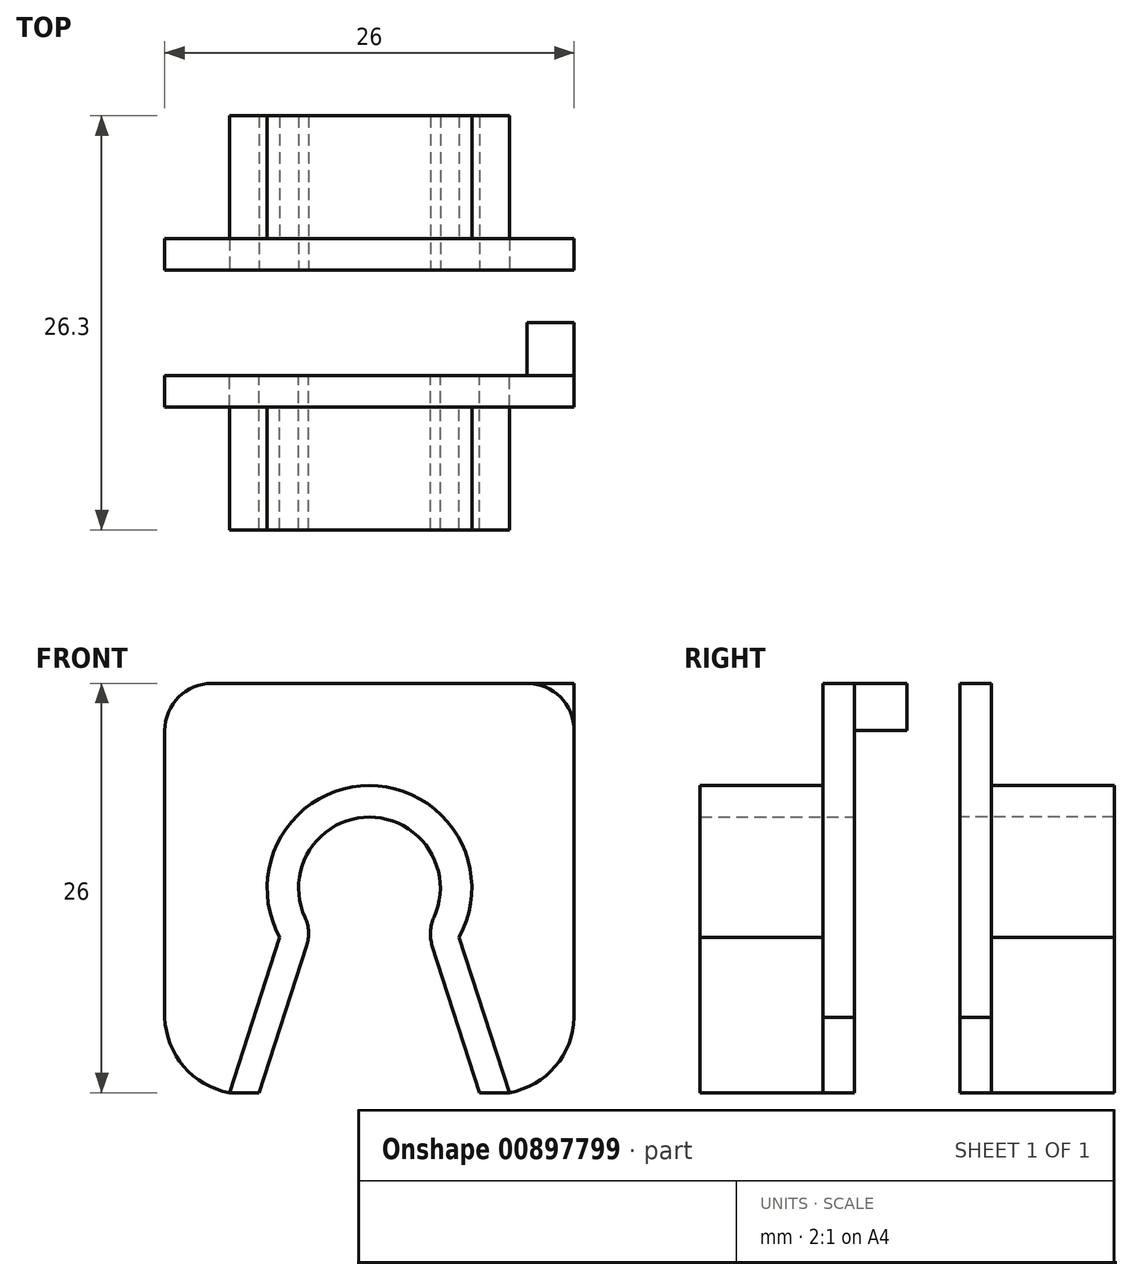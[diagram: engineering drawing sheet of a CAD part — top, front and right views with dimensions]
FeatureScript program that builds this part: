
annotation { "Feature Type Name" : "Feature", "Feature Type Description" : "" }
export const myFeature = defineFeature(function(context is Context, id is Id, definition is map)
    precondition{}
    {
        {
            var Q0;
            Q0=qCreatedBy(makeId("Front.planeOp"),FACE);
            var sketch = newSketch(context, id + "F0", { "sketchPlane" : qUnion([Q0])});
            skLineSegment(sketch, "E0.bottom", {"start": v(-13, 13) * mm, "end": v(13, 13) * mm});
            skLineSegment(sketch, "E0.top", {"start": v(-13, -13) * mm, "end": v(13, -13) * mm});
            skLineSegment(sketch, "E0.left", {"start": v(-13, 13) * mm, "end": v(-13, -13) * mm});
            skLineSegment(sketch, "E0.right", {"start": v(13, 13) * mm, "end": v(13, -13) * mm});
            skPoint(sketch, "E0.middle", {"position": v(0, 0) * mm});
            skCircle(sketch, "E1", {"center": v(0, 0) * mm, "radius": 4.5 * mm});
            skLineSegment(sketch, "E2", {"start": v(3.65, -2.63) * mm, "end": v(7, -13) * mm});
            skLineSegment(sketch, "E3", {"start": v(-3.65, -2.63) * mm, "end": v(-7, -13) * mm});
            skLineSegment(sketch, "E4", {"start": v(-4.42, 0.83) * mm, "end": v(-8.9, -13) * mm});
            skLineSegment(sketch, "E5", {"start": v(4.42, 0.83) * mm, "end": v(8.9, -13) * mm});
            skCircle(sketch, "E6", {"center": v(0, 0) * mm, "radius": 6.5 * mm});
            skLineSegment(sketch, "E7", {"start": v(-13, -8.21) * mm, "end": v(13, -8.21) * mm, "construction": true});
            skArc(sketch, "E8", {"start": v(-13, -8.21) * mm, "mid": v(-11.8, -11.34) * mm, "end": v(-8.9, -13) * mm});
            skArc(sketch, "E9", {"start": v(8.9, -13) * mm, "mid": v(11.8, -11.34) * mm, "end": v(13, -8.21) * mm});
            skSolve(sketch);
        }
        {
            var Q0;
            {var subQ0=sQuery(id+"F0.wireOp",EDGE,"E4");var subQ1=sQuery(id+"F0.wireOp",EDGE,"E1");var subQ2=makeQuery(id+"F0.imprint","INTERSECT",VERTEX,{"derivedFrom":[subQ1,subQ0]});Q0=makeQuery(id+"F0.imprint","IMPRINT",FACE,{"disambiguationData":[TD([[makeQuery(id+"F0.imprint","IMPRINT",EDGE,{"disambiguationData":[TD([[subQ2,1.0]])],"derivedFrom":subQ1}),-1.0]])]});}
            var Q1;
            {var subQ0=sQuery(id+"F0.wireOp",EDGE,"E3");var subQ1=sQuery(id+"F0.wireOp",EDGE,"E1");var subQ2=makeQuery(id+"F0.imprint","INTERSECT",VERTEX,{"derivedFrom":[subQ1,subQ0]});Q1=makeQuery(id+"F0.imprint","IMPRINT",FACE,{"disambiguationData":[TD([[makeQuery(id+"F0.imprint","IMPRINT",EDGE,{"disambiguationData":[TD([[subQ2,1.0]])],"derivedFrom":subQ1}),-1.0]])]});}
            var Q2;
            {var subQ0=sQuery(id+"F0.wireOp",EDGE,"E3");var subQ1=sQuery(id+"F0.wireOp",EDGE,"E0.top");var subQ2=makeQuery(id+"F0.imprint","INTERSECT",VERTEX,{"derivedFrom":[subQ1,subQ0]});Q2=makeQuery(id+"F0.imprint","IMPRINT",FACE,{"disambiguationData":[TD([[makeQuery(id+"F0.imprint","IMPRINT",EDGE,{"disambiguationData":[TD([[subQ2,1.0]])],"derivedFrom":subQ0}),-1.0]])]});}
            var Q3;
            {var subQ0=sQuery(id+"F0.wireOp",EDGE,"E2");var subQ1=sQuery(id+"F0.wireOp",EDGE,"E0.top");var subQ2=makeQuery(id+"F0.imprint","INTERSECT",VERTEX,{"derivedFrom":[subQ1,subQ0]});Q3=makeQuery(id+"F0.imprint","IMPRINT",FACE,{"disambiguationData":[TD([[makeQuery(id+"F0.imprint","IMPRINT",EDGE,{"disambiguationData":[TD([[subQ2,1.0]])],"derivedFrom":subQ0}),1.0]])]});}
            var Q4;
            {var subQ0=sQuery(id+"F0.wireOp",EDGE,"E2");var subQ1=sQuery(id+"F0.wireOp",EDGE,"E1");var subQ2=makeQuery(id+"F0.imprint","INTERSECT",VERTEX,{"derivedFrom":[subQ1,subQ0]});Q4=makeQuery(id+"F0.imprint","IMPRINT",FACE,{"disambiguationData":[TD([[makeQuery(id+"F0.imprint","IMPRINT",EDGE,{"disambiguationData":[TD([[subQ2,-1.0]])],"derivedFrom":subQ1}),-1.0]])]});}
            extrude(context, id + "F1", {"entities" : qUnion([Q0, Q1, Q2, Q3, Q4]), "depth" : 9.8 * mm, "offsetDistance" : 25 * mm});
        }
        {
            var Q0;
            {var subQ10=sQuery(id+"F0.wireOp",EDGE,"E0.bottom");Q0=makeQuery(id+"F0.imprint","IMPRINT",FACE,{"disambiguationData":[TD([[makeQuery(id+"F0.imprint","IMPRINT",EDGE,{"derivedFrom":subQ10}),-1.0]])]});}
            extrude(context, id + "F2", {"entities" : qUnion([Q0]), "operationType" : NewBodyOperationType.ADD, "depth" : 2 * mm, "offsetDistance" : 25 * mm});
        }
        {
            var Q0;
            Q0=makeQuery(id+"F2.opExtrude","SWEPT_EDGE",EDGE,{"disambiguationData":[OSD([sQuery(id+"F0.wireOp",EDGE,"E0.bottom"),sQuery(id+"F0.wireOp",EDGE,"E0.left")])]});
            var Q1;
            Q1=makeQuery(id+"F2.opExtrude","SWEPT_EDGE",EDGE,{"disambiguationData":[OSD([sQuery(id+"F0.wireOp",EDGE,"E0.bottom"),sQuery(id+"F0.wireOp",EDGE,"E0.right")])]});
            fillet(context, id + "F3", {"entities" : qUnion([Q0, Q1]), "radius" : 3 * mm, "tangentPropagation" : true, "allowEdgeOverflow" : false});
        }
        {
            var Q0;
            {var subQ10=sQuery(id+"F0.wireOp",EDGE,"E0.bottom");Q0=makeQuery(id+"F0.imprint","IMPRINT",FACE,{"disambiguationData":[TD([[makeQuery(id+"F0.imprint","IMPRINT",EDGE,{"derivedFrom":subQ10}),-1.0]])]});}
            var sketch = newSketch(context, id + "F4", { "sketchPlane" : qUnion([Q0])});
            skArc(sketch, "E10.0", {"start": v(10, 13) * mm, "mid": v(12.12, 12.12) * mm, "end": v(13, 10) * mm});
            skLineSegment(sketch, "E11.0", {"start": v(-13, 13) * mm, "end": v(13, 13) * mm});
            skPoint(sketch, "E12.0", {"position": v(-12.12, 12.12) * mm});
            skArc(sketch, "E13.0", {"start": v(-13, 10) * mm, "mid": v(-12.12, 12.12) * mm, "end": v(-10, 13) * mm});
            skLineSegment(sketch, "E14.0", {"start": v(13, 13) * mm, "end": v(13, -13) * mm});
            skLineSegment(sketch, "E15.0", {"start": v(-13, 13) * mm, "end": v(-13, -13) * mm});
            skLineSegment(sketch, "E16", {"start": v(13, 10) * mm, "end": v(-13, 10) * mm});
            skSolve(sketch);
        }
        {
            var Q0;
            {var subQ0=sQuery(id+"F4.wireOp",EDGE,"E11.0");var subQ1=sQuery(id+"F4.wireOp",EDGE,"E10.0");var subQ2=makeQuery(id+"F4.imprint","INTERSECT",VERTEX,{"derivedFrom":[subQ1,subQ0]});Q0=makeQuery(id+"F4.imprint","IMPRINT",FACE,{"disambiguationData":[TD([[makeQuery(id+"F4.imprint","IMPRINT",EDGE,{"disambiguationData":[TD([[subQ2,-1.0]])],"derivedFrom":subQ1}),-1.0]])]});}
            extrude(context, id + "F5", {"entities" : qUnion([Q0]), "operationType" : NewBodyOperationType.ADD, "oppositeDirection" : true, "depth" : (6.7 / 2) * mm, "offsetDistance" : 25 * mm});
        }
        {
            var Q0;
            Q0=makeQuery(id+"F1.opExtrude","SWEPT_BODY",BODY,{"disambiguationData":[OSD([sQuery(id+"F0.wireOp",EDGE,"E0.top"),sQuery(id+"F0.wireOp",EDGE,"E1"),sQuery(id+"F0.wireOp",EDGE,"E2"),sQuery(id+"F0.wireOp",EDGE,"E3"),sQuery(id+"F0.wireOp",EDGE,"E4"),sQuery(id+"F0.wireOp",EDGE,"E5"),sQuery(id+"F0.wireOp",EDGE,"E6")])]});
            var Q1;
            Q1=makeQuery(id+"F5.opExtrude","CAP_FACE",FACE,{"disambiguationData":[OSD([sQuery(id+"F4.wireOp",EDGE,"E10.0"),sQuery(id+"F4.wireOp",EDGE,"E11.0"),sQuery(id+"F4.wireOp",EDGE,"E13.0"),sQuery(id+"F4.wireOp",EDGE,"E16")])],"isStart":false});
            mirror(context, id + "F6", {"operationType" : NewBodyOperationType.ADD, "entities" : qUnion([Q0]), "mirrorPlane" : qUnion([Q1])});
        }
        {
            var Q0;
            Q0=makeQuery(id+"F1.opExtrude","SWEPT_EDGE",EDGE,{"disambiguationData":[OSD([sQuery(id+"F0.wireOp",EDGE,"E1"),sQuery(id+"F0.wireOp",EDGE,"E3")])]});
            var Q1;
            Q1=makeQuery(id+"F6.opPattern","COPY",EDGE,{"derivedFrom":makeQuery(id+"F1.opExtrude","SWEPT_EDGE",EDGE,{"disambiguationData":[OSD([sQuery(id+"F0.wireOp",EDGE,"E1"),sQuery(id+"F0.wireOp",EDGE,"E3")])]}),"instanceName":"1"});
            var Q2;
            Q2=makeQuery(id+"F6.opPattern","COPY",EDGE,{"derivedFrom":makeQuery(id+"F1.opExtrude","SWEPT_EDGE",EDGE,{"disambiguationData":[OSD([sQuery(id+"F0.wireOp",EDGE,"E1"),sQuery(id+"F0.wireOp",EDGE,"E2")])]}),"instanceName":"1"});
            var Q3;
            Q3=makeQuery(id+"F1.opExtrude","SWEPT_EDGE",EDGE,{"disambiguationData":[OSD([sQuery(id+"F0.wireOp",EDGE,"E1"),sQuery(id+"F0.wireOp",EDGE,"E2")])]});
            fillet(context, id + "F7", {"entities" : qUnion([Q0, Q1, Q2, Q3]), "radius" : 2.5 * mm, "tangentPropagation" : true, "allowEdgeOverflow" : false});
        }
    });
